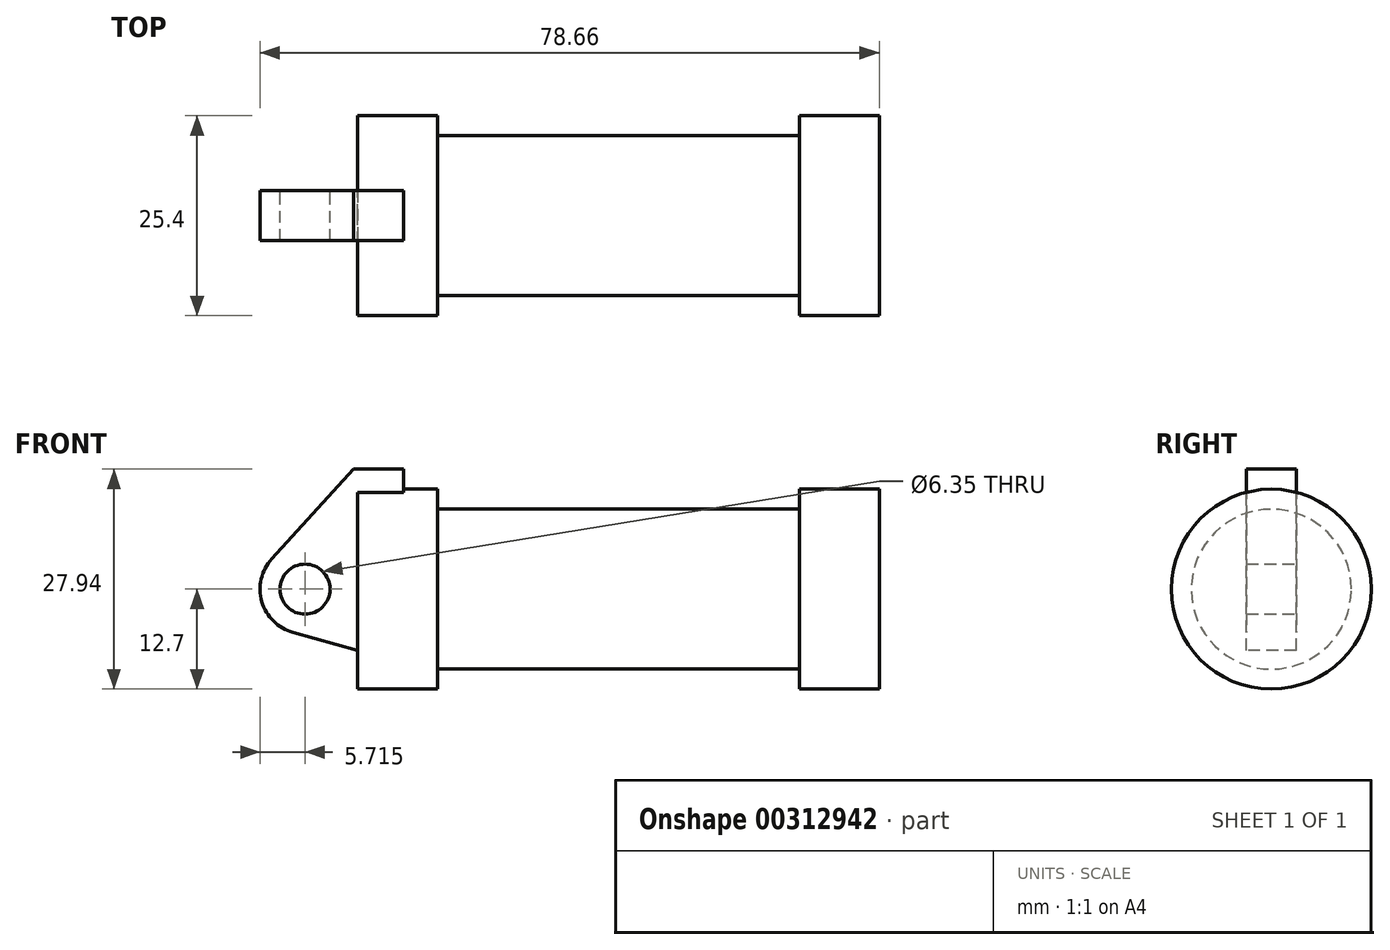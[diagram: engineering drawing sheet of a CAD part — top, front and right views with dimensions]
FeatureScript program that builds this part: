
annotation { "Feature Type Name" : "Feature", "Feature Type Description" : "" }
export const myFeature = defineFeature(function(context is Context, id is Id, definition is map)
    precondition{}
    {
        {
            var Q0;
            Q0=qCreatedBy(makeId("Front.planeOp"),FACE);
            var sketch = newSketch(context, id + "F0", { "sketchPlane" : qUnion([Q0])});
            skLineSegment(sketch, "E0", {"start": v(0, 0) * mm, "end": v(0, 12.7) * mm});
            skLineSegment(sketch, "E1", {"start": v(0, 12.7) * mm, "end": v(10.16, 12.7) * mm});
            skLineSegment(sketch, "E2", {"start": v(10.16, 12.7) * mm, "end": v(10.16, 10.16) * mm});
            skLineSegment(sketch, "E3", {"start": v(10.16, 10.16) * mm, "end": v(56.13, 10.16) * mm});
            skLineSegment(sketch, "E4", {"start": v(56.13, 10.16) * mm, "end": v(56.13, 12.7) * mm});
            skLineSegment(sketch, "E5", {"start": v(56.13, 12.7) * mm, "end": v(66.3, 12.7) * mm});
            skLineSegment(sketch, "E6", {"start": v(66.3, 12.7) * mm, "end": v(66.3, 0) * mm});
            skLineSegment(sketch, "E7", {"start": v(66.3, 0) * mm, "end": v(0, 0) * mm});
            skLineSegment(sketch, "E8", {"start": v(5.84, 15.24) * mm, "end": v(-0.5, 15.24) * mm});
            skLineSegment(sketch, "E9", {"start": v(-0.5, 15.24) * mm, "end": v(-10.88, 3.85) * mm});
            skLineSegment(sketch, "E10", {"start": v(0, 0) * mm, "end": v(-6.65, 0) * mm});
            skCircle(sketch, "E11", {"center": v(-6.65, 0) * mm, "radius": 5.72 * mm});
            skCircle(sketch, "E12", {"center": v(-6.65, 0) * mm, "radius": 3.18 * mm});
            skLineSegment(sketch, "E13", {"start": v(5.84, 15.24) * mm, "end": v(5.84, -9.4) * mm});
            skLineSegment(sketch, "E14", {"start": v(5.84, -9.4) * mm, "end": v(-8.18, -5.5) * mm});
            skSolve(sketch);
        }
        {
            var Q0;
            {var subQ1=sQuery(id+"F0.wireOp",EDGE,"E0");Q0=makeQuery(id+"F0.imprint","IMPRINT",FACE,{"disambiguationData":[TD([[makeQuery(id+"F0.imprint","IMPRINT",EDGE,{"derivedFrom":subQ1}),1.0]])]});}
            var Q1;
            {var subQ5=sQuery(id+"F0.wireOp",EDGE,"E12");Q1=makeQuery(id+"F0.imprint","IMPRINT",FACE,{"disambiguationData":[TD([[makeQuery(id+"F0.imprint","IMPRINT",EDGE,{"derivedFrom":subQ5}),-1.0]])]});}
            var Q2;
            {var subQ0=sQuery(id+"F0.wireOp",EDGE,"E14");Q2=makeQuery(id+"F0.imprint","IMPRINT",FACE,{"disambiguationData":[TD([[makeQuery(id+"F0.imprint","IMPRINT",EDGE,{"derivedFrom":subQ0}),-1.0]])]});}
            var Q3;
            {var subQ0=sQuery(id+"F0.wireOp",EDGE,"E0");Q3=makeQuery(id+"F0.imprint","IMPRINT",FACE,{"disambiguationData":[TD([[makeQuery(id+"F0.imprint","IMPRINT",EDGE,{"derivedFrom":subQ0}),-1.0]])]});}
            extrude(context, id + "F1", {"entities" : qUnion([Q0, Q1, Q2, Q3]), "endBound" : BoundingType.SYMMETRIC, "depth" : 6.35 * mm});
        }
        {
            var Q0;
            {var subQ0=sQuery(id+"F0.wireOp",EDGE,"E2");Q0=makeQuery(id+"F0.imprint","IMPRINT",FACE,{"disambiguationData":[TD([[makeQuery(id+"F0.imprint","IMPRINT",EDGE,{"derivedFrom":subQ0}),-1.0]])]});}
            var Q1;
            {var subQ0=sQuery(id+"F0.wireOp",EDGE,"E0");Q1=makeQuery(id+"F0.imprint","IMPRINT",FACE,{"disambiguationData":[TD([[makeQuery(id+"F0.imprint","IMPRINT",EDGE,{"derivedFrom":subQ0}),-1.0]])]});}
            var Q2;
            Q2=sQuery(id+"F0.wireOp",EDGE,"E7");
            revolve(context, id + "F2", {"operationType" : NewBodyOperationType.ADD, "entities" : qUnion([Q0, Q1]), "axis" : qUnion([Q2]), "revolveType" : RevolveType.FULL});
        }
    });
